annotation { "Feature Type Name" : "Feature", "Feature Type Description" : "" }
export const myFeature = defineFeature(function(context is Context, id is Id, definition is map)
    precondition{}
    {
        {
            var Q0;
            Q0=qCreatedBy(makeId("Top.planeOp"),FACE);
            var sketch = newSketch(context, id + "F0", { "sketchPlane" : qUnion([Q0])});
            skLineSegment(sketch, "E0.bottom", {"start": v(0, 0) * mm, "end": v(57.74, 0) * mm});
            skLineSegment(sketch, "E0.top", {"start": v(0, -20.58) * mm, "end": v(57.74, -20.58) * mm});
            skLineSegment(sketch, "E0.left", {"start": v(0, 0) * mm, "end": v(0, -20.58) * mm});
            skLineSegment(sketch, "E0.right", {"start": v(57.74, 0) * mm, "end": v(57.74, -20.58) * mm});
            skSolve(sketch);
        }
        {
            var Q0;
            Q0=makeQuery(id+"F0.imprint","IMPRINT",FACE,{"disambiguationData":[TD([[makeQuery(id+"F0.imprint","IMPRINT",EDGE,{"derivedFrom":sQuery(id+"F0.wireOp",EDGE,"E0.bottom")}),-1.0]])]});
            extrude(context, id + "F1", {"entities" : qUnion([Q0]), "depth" : 3.8 * mm, "offsetDistance" : 25.4 * mm});
        }
        {
            var Q0;
            Q0=makeQuery(id+"F1.opExtrude","CAP_FACE",FACE,{"disambiguationData":[OSD([sQuery(id+"F0.wireOp",EDGE,"E0.bottom"),sQuery(id+"F0.wireOp",EDGE,"E0.top"),sQuery(id+"F0.wireOp",EDGE,"E0.left"),sQuery(id+"F0.wireOp",EDGE,"E0.right")])],"isStart":false});
            var sketch = newSketch(context, id + "F2", { "sketchPlane" : qUnion([Q0])});
            skLineSegment(sketch, "E1", {"start": v(15.16, -7.36) * mm, "end": v(12.9, -7.36) * mm});
            skLineSegment(sketch, "E2", {"start": v(15.16, -7.36) * mm, "end": v(15.16, -3.34) * mm});
            skLineSegment(sketch, "E3", {"start": v(15.16, -3.34) * mm, "end": v(12.79, -3.34) * mm});
            skLineSegment(sketch, "E4", {"start": v(12.79, -3.34) * mm, "end": v(12.79, -4.42) * mm});
            skLineSegment(sketch, "E5", {"start": v(10.28, -7.74) * mm, "end": v(10.28, -11.42) * mm});
            skLineSegment(sketch, "E6", {"start": v(10.28, -11.42) * mm, "end": v(12.37, -11.42) * mm});
            skLineSegment(sketch, "E7", {"start": v(12.37, -11.42) * mm, "end": v(12.57, -10.46) * mm});
            skLineSegment(sketch, "E8", {"start": v(10.28, -7.74) * mm, "end": v(23.96, -7.74) * mm});
            skLineSegment(sketch, "E9", {"start": v(23.96, -7.74) * mm, "end": v(24.04, -11.41) * mm});
            skLineSegment(sketch, "E10", {"start": v(24.04, -11.41) * mm, "end": v(21.9, -11.46) * mm});
            skLineSegment(sketch, "E11", {"start": v(21.9, -11.46) * mm, "end": v(21.69, -10.34) * mm});
            skLineSegment(sketch, "E12", {"start": v(21.69, -10.34) * mm, "end": v(19.04, -10.34) * mm});
            skLineSegment(sketch, "E13", {"start": v(19.04, -10.34) * mm, "end": v(19.04, -14.95) * mm});
            skLineSegment(sketch, "E14", {"start": v(19.04, -14.95) * mm, "end": v(20.32, -14.95) * mm});
            skLineSegment(sketch, "E15", {"start": v(20.32, -14.95) * mm, "end": v(20.32, -17.33) * mm});
            skLineSegment(sketch, "E16", {"start": v(20.32, -17.33) * mm, "end": v(14.71, -17.33) * mm});
            skLineSegment(sketch, "E17", {"start": v(14.71, -17.33) * mm, "end": v(14.71, -14.99) * mm});
            skLineSegment(sketch, "E18", {"start": v(14.71, -14.99) * mm, "end": v(16.04, -14.99) * mm});
            skLineSegment(sketch, "E19", {"start": v(16.04, -14.99) * mm, "end": v(16.04, -10.34) * mm});
            skLineSegment(sketch, "E20", {"start": v(16.04, -10.34) * mm, "end": v(15.32, -10.34) * mm});
            skLineSegment(sketch, "E21", {"start": v(15.32, -10.34) * mm, "end": v(15.32, -14.43) * mm});
            skLineSegment(sketch, "E22", {"start": v(15.32, -14.43) * mm, "end": v(12.88, -14.43) * mm});
            skLineSegment(sketch, "E23", {"start": v(12.88, -14.43) * mm, "end": v(12.88, -14.1) * mm});
            skArc(sketch, "E24", {"start": v(12.9, -7.36) * mm, "mid": v(9.73, -5.92) * mm, "end": v(6.37, -6.86) * mm});
            skArc(sketch, "E25", {"start": v(12.79, -4.42) * mm, "mid": v(7.86, -3.35) * mm, "end": v(3.28, -5.48) * mm});
            skArc(sketch, "E26", {"start": v(3.28, -5.48) * mm, "mid": v(1.55, -8.98) * mm, "end": v(2.78, -12.68) * mm});
            skArc(sketch, "E27", {"start": v(2.78, -12.68) * mm, "mid": v(7.6, -15.06) * mm, "end": v(12.88, -14.1) * mm});
            skPoint(sketch, "E28.end.orphan", {"position": v(13.45, -10.46) * mm});
            skPoint(sketch, "E29.end.orphan", {"position": v(13.17, -10.46) * mm});
            skLineSegment(sketch, "E30", {"start": v(12.57, -10.46) * mm, "end": v(13.45, -10.46) * mm});
            skArc(sketch, "E31", {"start": v(6.37, -6.86) * mm, "mid": v(5.04, -9.47) * mm, "end": v(6.52, -12) * mm});
            skArc(sketch, "E32", {"start": v(6.52, -12) * mm, "mid": v(9.01, -12.74) * mm, "end": v(11.57, -12.3) * mm});
            skArc(sketch, "E33", {"start": v(11.57, -12.3) * mm, "mid": v(12.53, -11.52) * mm, "end": v(13.17, -10.46) * mm});
            skSolve(sketch);
        }
        {
            var Q0;
            Q0=makeQuery(id+"F2.imprint","IMPRINT",FACE,{"disambiguationData":[TD([[makeQuery(id+"F2.imprint","IMPRINT",EDGE,{"derivedFrom":sQuery(id+"F2.wireOp",EDGE,"E1")}),-1.0]])]});
            extrude(context, id + "F3", {"entities" : qUnion([Q0]), "operationType" : NewBodyOperationType.REMOVE, "flatOperationType" : FlatOperationType.REMOVE, "oppositeDirection" : true, "depth" : 2.54 * mm, "offsetDistance" : 25.4 * mm, "domain" : OperationDomain.MODEL});
        }
        {
            var Q0;
            Q0=makeQuery(id+"F1.opExtrude","SWEPT_EDGE",EDGE,{"disambiguationData":[OSD([sQuery(id+"F0.wireOp",EDGE,"E0.top"),sQuery(id+"F0.wireOp",EDGE,"E0.right")])]});
            var Q1;
            Q1=makeQuery(id+"F1.opExtrude","SWEPT_EDGE",EDGE,{"disambiguationData":[OSD([sQuery(id+"F0.wireOp",EDGE,"E0.bottom"),sQuery(id+"F0.wireOp",EDGE,"E0.right")])]});
            chamfer(context, id + "F4", {"entities" : qUnion([Q0, Q1]), "width" : 5.08 * mm, "tangentPropagation" : true});
        }
        {
            var Q0;
            Q0=makeQuery(id+"F1.opExtrude","SWEPT_EDGE",EDGE,{"disambiguationData":[OSD([sQuery(id+"F0.wireOp",EDGE,"E0.top"),sQuery(id+"F0.wireOp",EDGE,"E0.left")])]});
            var Q1;
            Q1=makeQuery(id+"F1.opExtrude","SWEPT_EDGE",EDGE,{"disambiguationData":[OSD([sQuery(id+"F0.wireOp",EDGE,"E0.bottom"),sQuery(id+"F0.wireOp",EDGE,"E0.left")])]});
            fillet(context, id + "F5", {"entities" : qUnion([Q0, Q1]), "radius" : 5.08 * mm, "tangentPropagation" : true, "allowEdgeOverflow" : false});
        }
        {
            var Q0;
            Q0=makeQuery(id+"F1.opExtrude","CAP_FACE",FACE,{"disambiguationData":[OSD([sQuery(id+"F0.wireOp",EDGE,"E0.bottom"),sQuery(id+"F0.wireOp",EDGE,"E0.top"),sQuery(id+"F0.wireOp",EDGE,"E0.left"),sQuery(id+"F0.wireOp",EDGE,"E0.right")])],"isStart":false});
            var sketch = newSketch(context, id + "F6", { "sketchPlane" : qUnion([Q0])});
            skText(sketch, "E34", { "text": "Allen Ayala\nGTRI ATAS Intern ", "fontName": "OpenSans-Regular.ttf"});
            const initialGuessF6  = {"E34": [0.02794, -0.00867, 1, 0, 0.00232]};
            skSetInitialGuess(sketch, initialGuessF6);
            skSolve(sketch);
        }
        {
            var Q0;
            Q0=qCreatedBy(makeId("Top.planeOp"),FACE);
            var sketch = newSketch(context, id + "F7", { "sketchPlane" : qUnion([Q0])});
            skLineSegment(sketch, "E35.bottom", {"start": v(0, -7.4) * mm, "end": v(-5.2, -7.4) * mm});
            skLineSegment(sketch, "E35.top", {"start": v(0, -12.47) * mm, "end": v(-5.2, -12.47) * mm});
            skLineSegment(sketch, "E35.left", {"start": v(0, -7.4) * mm, "end": v(0, -12.47) * mm});
            skLineSegment(sketch, "E35.right", {"start": v(-5.2, -7.4) * mm, "end": v(-5.2, -12.47) * mm});
            skCircle(sketch, "E36", {"center": v(-2.68, -9.83) * mm, "radius": 1.78 * mm});
            skSolve(sketch);
        }
        {
            var Q0;
            Q0=makeQuery(id+"F7.imprint","IMPRINT",FACE,{"disambiguationData":[TD([[makeQuery(id+"F7.imprint","IMPRINT",EDGE,{"derivedFrom":sQuery(id+"F7.wireOp",EDGE,"E35.bottom")}),1.0]])]});
            extrude(context, id + "F8", {"entities" : qUnion([Q0]), "operationType" : NewBodyOperationType.ADD, "depth" : 3.8 * mm, "offsetDistance" : 25.4 * mm});
        }
        {
            var Q0;
            Q0 = qSketchRegion(id + "F6", true);
            extrude(context, id + "F9", {"entities" : qUnion([Q0]), "operationType" : NewBodyOperationType.REMOVE, "oppositeDirection" : true, "depth" : 2.54 * mm, "offsetDistance" : 25.4 * mm});
        }
    });